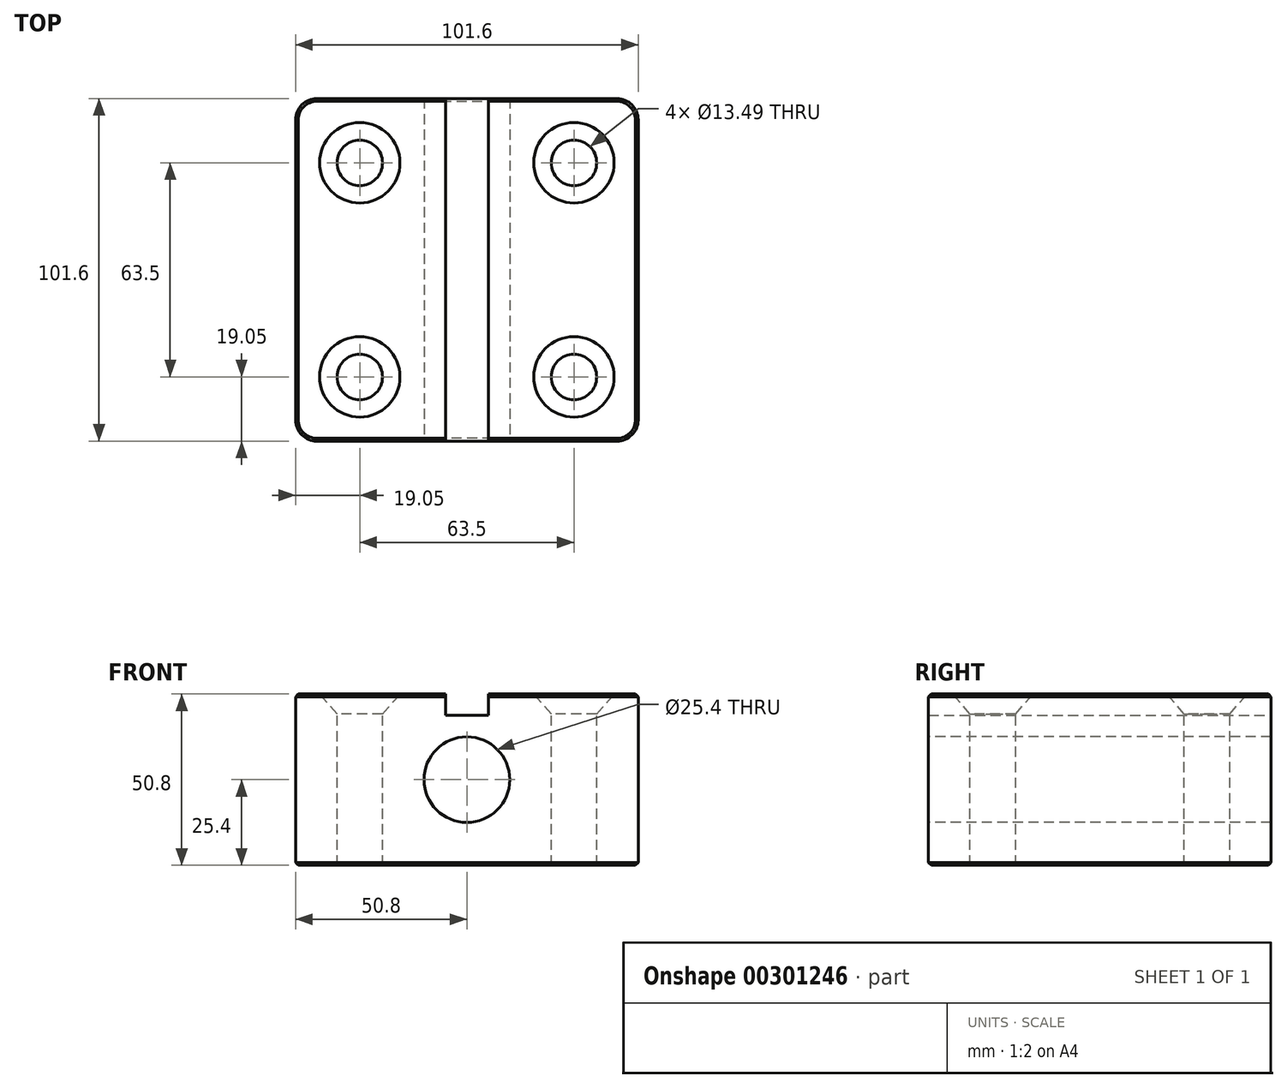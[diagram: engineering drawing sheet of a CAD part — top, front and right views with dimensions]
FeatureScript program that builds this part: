
annotation { "Feature Type Name" : "Feature", "Feature Type Description" : "" }
export const myFeature = defineFeature(function(context is Context, id is Id, definition is map)
    precondition{}
    {
        {
            var Q0;
            Q0=qCreatedBy(makeId("Front.planeOp"),FACE);
            var sketch = newSketch(context, id + "F0", { "sketchPlane" : qUnion([Q0])});
            skLineSegment(sketch, "E0.bottom", {"start": v(-50.8, 25.4) * mm, "end": v(50.8, 25.4) * mm});
            skLineSegment(sketch, "E0.top", {"start": v(-50.8, -25.4) * mm, "end": v(50.8, -25.4) * mm});
            skLineSegment(sketch, "E0.left", {"start": v(-50.8, 25.4) * mm, "end": v(-50.8, -25.4) * mm});
            skLineSegment(sketch, "E0.right", {"start": v(50.8, 25.4) * mm, "end": v(50.8, -25.4) * mm});
            skLineSegment(sketch, "E1.bottom", {"start": v(-6.35, 25.4) * mm, "end": v(6.35, 25.4) * mm});
            skLineSegment(sketch, "E1.top", {"start": v(-6.35, 19.05) * mm, "end": v(6.35, 19.05) * mm});
            skLineSegment(sketch, "E1.left", {"start": v(-6.35, 25.4) * mm, "end": v(-6.35, 19.05) * mm});
            skLineSegment(sketch, "E1.right", {"start": v(6.35, 25.4) * mm, "end": v(6.35, 19.05) * mm});
            skSolve(sketch);
        }
        {
            var Q0;
            Q0=makeQuery(id+"F0.imprint","IMPRINT",FACE,{"disambiguationData":[TD([[makeQuery(id+"F0.imprint","IMPRINT",EDGE,{"derivedFrom":sQuery(id+"F0.wireOp",EDGE,"E0.bottom")}),-1.0]])]});
            extrude(context, id + "F1", {"entities" : qUnion([Q0]), "endBound" : BoundingType.SYMMETRIC, "depth" : 101.6 * mm});
        }
        {
            var Q0;
            Q0=makeQuery(id+"F1.opExtrude","SWEPT_FACE",FACE,{"disambiguationData":[OSD([sQuery(id+"F0.wireOp",EDGE,"E0.bottom")])]});
            var sketch = newSketch(context, id + "F2", { "sketchPlane" : qUnion([Q0])});
            skPoint(sketch, "E2", {"position": v(-31.75, 31.75) * mm});
            skPoint(sketch, "E3.MirrorP", {"position": v(31.75, 31.75) * mm});
            skPoint(sketch, "E4.MirrorP", {"position": v(31.75, -31.75) * mm});
            skPoint(sketch, "E5.MirrorP", {"position": v(-31.75, -31.75) * mm});
            skSolve(sketch);
        }
        {
            var Q0;
            Q0=sQuery(id+"F2.wireOp",VERTEX,"E2");
            var Q1;
            Q1=sQuery(id+"F2.wireOp",VERTEX,"E3.MirrorP");
            var Q2;
            Q2=sQuery(id+"F2.wireOp",VERTEX,"E4.MirrorP");
            var Q3;
            Q3=sQuery(id+"F2.wireOp",VERTEX,"E5.MirrorP");
            var Q4;
            Q4=makeQuery(id+"F1.opExtrude","SWEPT_BODY",BODY,{"disambiguationData":[OSD([sQuery(id+"F0.wireOp",EDGE,"E0.bottom"),sQuery(id+"F0.wireOp",EDGE,"E0.top"),sQuery(id+"F0.wireOp",EDGE,"E0.left"),sQuery(id+"F0.wireOp",EDGE,"E0.right")])]});
            hole(context, id + "F3", {"style" : HoleStyle.C_SINK, "endStyle" : HoleEndStyle.THROUGH, "standardTappedOrClearance" : lookupTablePath({ "standard" : "ANSI", "fit" : "Normal (ASME)", "size" : "1/2", "type" : "Clearance" }), "standardBlindInLast" : lookupTablePath({ "fit" : "Free", "standard" : "ANSI", "size" : "1/2", "type" : "Clearance" }), "holeDiameter" : 13.5 * mm, "cSinkDiameter" : 23.83 * mm, "cSinkAngle" : 82 * degree, "tappedDepth" : 12.7 * mm, "tapClearance" : 3, "locations" : qUnion([Q0, Q1, Q2, Q3]), "scope" : qUnion([Q4])});
        }
        {
            var Q0;
            Q0=makeQuery(id+"F1.opExtrude","CAP_EDGE",EDGE,{"disambiguationData":[OSD([sQuery(id+"F0.wireOp",EDGE,"E0.right")])],"isStart":false});
            var Q1;
            Q1=makeQuery(id+"F1.opExtrude","CAP_EDGE",EDGE,{"disambiguationData":[OSD([sQuery(id+"F0.wireOp",EDGE,"E0.left")])],"isStart":false});
            var Q2;
            Q2=makeQuery(id+"F1.opExtrude","CAP_EDGE",EDGE,{"disambiguationData":[OSD([sQuery(id+"F0.wireOp",EDGE,"E0.left")])],"isStart":true});
            var Q3;
            Q3=makeQuery(id+"F1.opExtrude","CAP_EDGE",EDGE,{"disambiguationData":[OSD([sQuery(id+"F0.wireOp",EDGE,"E0.right")])],"isStart":true});
            fillet(context, id + "F4", {"entities" : qUnion([Q0, Q1, Q2, Q3]), "radius" : 6.35 * mm, "tangentPropagation" : true, "allowEdgeOverflow" : false});
        }
        {
            var Q0;
            {var subQ0=sQuery(id+"F0.wireOp",EDGE,"E0.bottom");Q0=makeQuery(id+"F1.opExtrude","CAP_EDGE",EDGE,{"disambiguationData":[OSD([subQ0]),TDD([makeQuery(id+"F0.imprint","IMPRINT",EDGE,{"disambiguationData":[TD([[makeQuery(id+"F0.imprint","INTERSECT",VERTEX,{"derivedFrom":[subQ0,sQuery(id+"F0.wireOp",EDGE,"E0.right")]}),1.0]])],"derivedFrom":subQ0})])],"isStart":false});}
            var Q1;
            Q1=makeQuery(id+"F1.opExtrude","SWEPT_EDGE",EDGE,{"disambiguationData":[OSD([sQuery(id+"F0.wireOp",EDGE,"E0.bottom"),sQuery(id+"F0.wireOp",EDGE,"E0.left")])]});
            var Q2;
            Q2=makeQuery(id+"F1.opExtrude","CAP_EDGE",EDGE,{"disambiguationData":[OSD([sQuery(id+"F0.wireOp",EDGE,"E0.top")])],"isStart":true});
            chamfer(context, id + "F5", {"entities" : qUnion([Q0, Q1, Q2]), "width" : 0.81 * mm, "tangentPropagation" : true});
        }
        {
            var Q0;
            Q0=makeQuery(id+"F1.opExtrude","CAP_FACE",FACE,{"disambiguationData":[OSD([sQuery(id+"F0.wireOp",EDGE,"E0.bottom"),sQuery(id+"F0.wireOp",EDGE,"E0.top"),sQuery(id+"F0.wireOp",EDGE,"E0.left"),sQuery(id+"F0.wireOp",EDGE,"E0.right")])],"isStart":false});
            var sketch = newSketch(context, id + "F6", { "sketchPlane" : qUnion([Q0])});
            skPoint(sketch, "E6", {"position": v(0, 0) * mm});
            skSolve(sketch);
        }
        {
            var Q0;
            Q0=sQuery(id+"F6.wireOp",VERTEX,"E6");
            var Q1;
            Q1=makeQuery(id+"F1.opExtrude","SWEPT_BODY",BODY,{"disambiguationData":[OSD([sQuery(id+"F0.wireOp",EDGE,"E0.bottom"),sQuery(id+"F0.wireOp",EDGE,"E0.top"),sQuery(id+"F0.wireOp",EDGE,"E0.left"),sQuery(id+"F0.wireOp",EDGE,"E0.right")])]});
            hole(context, id + "F7", {"style" : HoleStyle.SIMPLE, "endStyle" : HoleEndStyle.THROUGH, "holeDiameter" : 25.4 * mm, "tappedDepth" : 12.7 * mm, "tapClearance" : 3, "locations" : qUnion([Q0]), "scope" : qUnion([Q1])});
        }
    });
